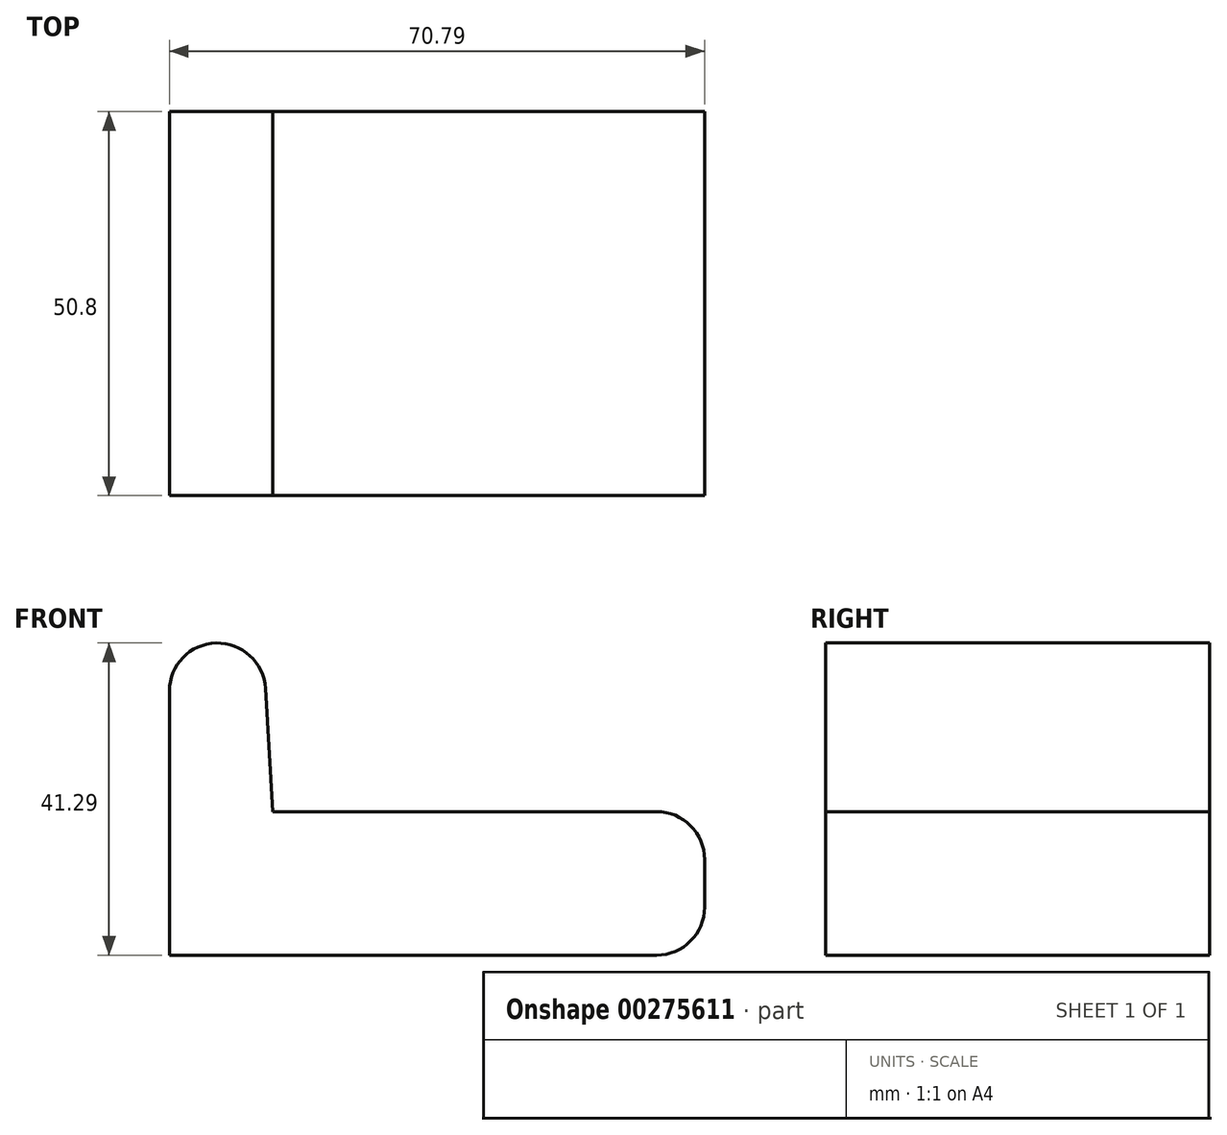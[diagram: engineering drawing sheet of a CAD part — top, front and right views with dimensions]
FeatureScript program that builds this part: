
annotation { "Feature Type Name" : "Feature", "Feature Type Description" : "" }
export const myFeature = defineFeature(function(context is Context, id is Id, definition is map)
    precondition{}
    {
        {
            var Q0;
            Q0=qCreatedBy(makeId("Front.planeOp"),FACE);
            var sketch = newSketch(context, id + "F0", { "sketchPlane" : qUnion([Q0])});
            skLineSegment(sketch, "E0", {"start": v(-30.05, -1.2) * mm, "end": v(-30.05, -36.13) * mm});
            skLineSegment(sketch, "E1", {"start": v(-30.05, -36.13) * mm, "end": v(34.4, -36.13) * mm});
            skLineSegment(sketch, "E2", {"start": v(40.74, -29.78) * mm, "end": v(40.74, -23.5) * mm});
            skLineSegment(sketch, "E3", {"start": v(34.4, -17.15) * mm, "end": v(-16.4, -17.15) * mm});
            skLineSegment(sketch, "E4", {"start": v(-16.4, -17.15) * mm, "end": v(-17.36, -0.82) * mm});
            skPoint(sketch, "E5.visualSharp", {"position": v(40.74, -36.13) * mm});
            skArc(sketch, "E5.filletArc", {"start": v(34.4, -36.13) * mm, "mid": v(38.88, -34.27) * mm, "end": v(40.74, -29.78) * mm});
            skPoint(sketch, "E6.visualSharp", {"position": v(40.74, -17.15) * mm});
            skArc(sketch, "E6.filletArc", {"start": v(40.74, -23.5) * mm, "mid": v(38.88, -19) * mm, "end": v(34.4, -17.15) * mm});
            skPoint(sketch, "E7.visualSharp", {"position": v(-30.05, 216.5) * mm});
            skArc(sketch, "E7.filletArc", {"start": v(-17.36, -0.82) * mm, "mid": v(-23.88, 5.16) * mm, "end": v(-30.05, -1.2) * mm});
            skSolve(sketch);
        }
        {
            var Q0;
            Q0=makeQuery(id+"F0.imprint","IMPRINT",FACE,{"disambiguationData":[TD([[makeQuery(id+"F0.imprint","IMPRINT",EDGE,{"derivedFrom":sQuery(id+"F0.wireOp",EDGE,"E0")}),1.0]])]});
            extrude(context, id + "F1", {"entities" : qUnion([Q0]), "depth" : 50.8 * mm});
        }
    });
